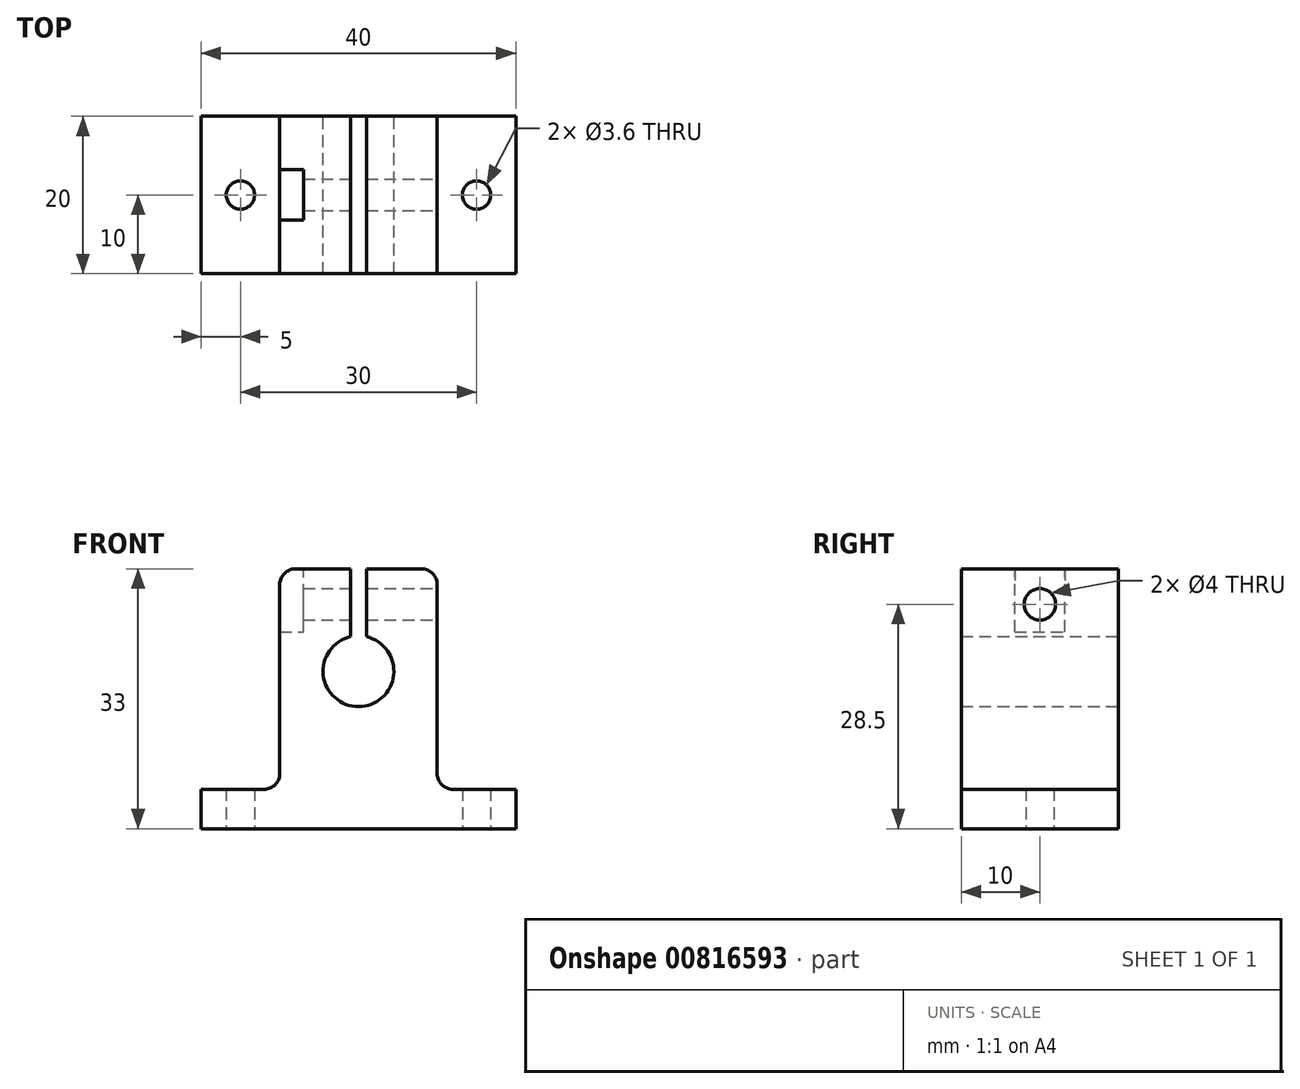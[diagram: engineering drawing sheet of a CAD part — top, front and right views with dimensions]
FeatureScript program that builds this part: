
annotation { "Feature Type Name" : "Feature", "Feature Type Description" : "" }
export const myFeature = defineFeature(function(context is Context, id is Id, definition is map)
    precondition{}
    {
        {
            var Q0;
            Q0=qCreatedBy(makeId("Front.planeOp"),FACE);
            var sketch = newSketch(context, id + "F0", { "sketchPlane" : qUnion([Q0])});
            skLineSegment(sketch, "E0", {"start": v(-10, 33) * mm, "end": v(10, 33) * mm});
            skLineSegment(sketch, "E1", {"start": v(10, 33) * mm, "end": v(10, 5) * mm});
            skLineSegment(sketch, "E2", {"start": v(10, 5) * mm, "end": v(20, 5) * mm});
            skLineSegment(sketch, "E3", {"start": v(20, 5) * mm, "end": v(20, 0) * mm});
            skLineSegment(sketch, "E4", {"start": v(20, 0) * mm, "end": v(-20, 0) * mm});
            skLineSegment(sketch, "E5", {"start": v(-20, 0) * mm, "end": v(-20, 5) * mm});
            skLineSegment(sketch, "E6", {"start": v(-20, 5) * mm, "end": v(-10, 5) * mm});
            skLineSegment(sketch, "E7", {"start": v(-10, 5) * mm, "end": v(-10, 33) * mm});
            skLineSegment(sketch, "E8", {"start": v(0, 33) * mm, "end": v(0, 0) * mm, "construction": true});
            skLineSegment(sketch, "E9", {"start": v(-1, 33) * mm, "end": v(-1, 20) * mm});
            skLineSegment(sketch, "E10", {"start": v(-1, 20) * mm, "end": v(0, 20) * mm});
            skCircle(sketch, "E11", {"center": v(0, 20) * mm, "radius": 4.5 * mm});
            skLineSegment(sketch, "E12.MirrorCS", {"start": v(1, 33) * mm, "end": v(1, 20) * mm});
            skLineSegment(sketch, "E13.MirrorCS", {"start": v(1, 20) * mm, "end": v(0, 20) * mm});
            skSolve(sketch);
        }
        {
            var Q0;
            {var subQ6=sQuery(id+"F0.wireOp",EDGE,"E1");Q0=makeQuery(id+"F0.imprint","IMPRINT",FACE,{"disambiguationData":[TD([[makeQuery(id+"F0.imprint","IMPRINT",EDGE,{"derivedFrom":subQ6}),-1.0]])]});}
            extrude(context, id + "F1", {"entities" : qUnion([Q0]), "depth" : 20 * mm, "offsetDistance" : 25 * mm});
        }
        {
            var Q0;
            Q0=makeQuery(id+"F1.opExtrude","SWEPT_FACE",FACE,{"disambiguationData":[OSD([sQuery(id+"F0.wireOp",EDGE,"E1")])]});
            var sketch = newSketch(context, id + "F2", { "sketchPlane" : qUnion([Q0])});
            skCircle(sketch, "E14", {"center": v(-10, 28.5) * mm, "radius": 2 * mm});
            skPoint(sketch, "E14.centerSnap0", {"position": v(-10, 33) * mm});
            skSolve(sketch);
        }
        {
            var Q0;
            Q0=makeQuery(id+"F2.imprint","IMPRINT",FACE,{"disambiguationData":[TD([[makeQuery(id+"F2.imprint","IMPRINT",EDGE,{"derivedFrom":sQuery(id+"F2.wireOp",EDGE,"E14")}),1.0]])]});
            extrude(context, id + "F3", {"entities" : qUnion([Q0]), "operationType" : NewBodyOperationType.REMOVE, "oppositeDirection" : true, "depth" : 25 * mm, "offsetDistance" : 25 * mm});
        }
        {
            var Q0;
            {var subQ0=sQuery(id+"F0.wireOp",EDGE,"E0");Q0=makeQuery(id+"F1.opExtrude","SWEPT_FACE",FACE,{"disambiguationData":[OSD([subQ0]),TDD([makeQuery(id+"F0.imprint","IMPRINT",EDGE,{"disambiguationData":[TD([[makeQuery(id+"F0.imprint","INTERSECT",VERTEX,{"derivedFrom":[subQ0,sQuery(id+"F0.wireOp",EDGE,"E7")]}),-1.0]])],"derivedFrom":subQ0})])]});}
            var sketch = newSketch(context, id + "F4", { "sketchPlane" : qUnion([Q0])});
            skLineSegment(sketch, "E15", {"start": v(-10, -10) * mm, "end": v(-1, -10) * mm, "construction": true});
            skLineSegment(sketch, "E16", {"start": v(-10, -6.8) * mm, "end": v(-7, -6.8) * mm});
            skLineSegment(sketch, "E17", {"start": v(-7, -6.8) * mm, "end": v(-7, -10) * mm});
            skLineSegment(sketch, "E18.MirrorCS", {"start": v(-7, -13.2) * mm, "end": v(-7, -10) * mm});
            skLineSegment(sketch, "E19.MirrorCS", {"start": v(-10, -13.2) * mm, "end": v(-7, -13.2) * mm});
            skSolve(sketch);
        }
        {
            var Q0;
            {var subQ1=sQuery(id+"F4.wireOp",EDGE,"E16");Q0=makeQuery(id+"F4.imprint","IMPRINT",FACE,{"disambiguationData":[TD([[makeQuery(id+"F4.imprint","IMPRINT",EDGE,{"derivedFrom":subQ1}),-1.0]])]});}
            extrude(context, id + "F5", {"entities" : qUnion([Q0]), "operationType" : NewBodyOperationType.REMOVE, "oppositeDirection" : true, "depth" : 8 * mm, "offsetDistance" : 25 * mm});
        }
        {
            var Q0;
            Q0=makeQuery(id+"F1.opExtrude","SWEPT_FACE",FACE,{"disambiguationData":[OSD([sQuery(id+"F0.wireOp",EDGE,"E4")])]});
            var sketch = newSketch(context, id + "F6", { "sketchPlane" : qUnion([Q0])});
            skLineSegment(sketch, "E20", {"start": v(-20, 10) * mm, "end": v(20, 10) * mm, "construction": true});
            skCircle(sketch, "E21", {"center": v(-15, 10) * mm, "radius": 1.8 * mm});
            skCircle(sketch, "E22", {"center": v(15, 10) * mm, "radius": 1.8 * mm});
            skSolve(sketch);
        }
        {
            var Q0;
            Q0=makeQuery(id+"F6.imprint","IMPRINT",FACE,{"disambiguationData":[TD([[makeQuery(id+"F6.imprint","IMPRINT",EDGE,{"derivedFrom":sQuery(id+"F6.wireOp",EDGE,"E21")}),1.0]])]});
            var Q1;
            Q1=makeQuery(id+"F6.imprint","IMPRINT",FACE,{"disambiguationData":[TD([[makeQuery(id+"F6.imprint","IMPRINT",EDGE,{"derivedFrom":sQuery(id+"F6.wireOp",EDGE,"E22")}),1.0]])]});
            extrude(context, id + "F7", {"entities" : qUnion([Q0, Q1]), "operationType" : NewBodyOperationType.REMOVE, "oppositeDirection" : true, "depth" : 25 * mm, "offsetDistance" : 25 * mm});
        }
        {
            var Q0;
            Q0=makeQuery(id+"F1.opExtrude","SWEPT_EDGE",EDGE,{"disambiguationData":[OSD([sQuery(id+"F0.wireOp",EDGE,"E6"),sQuery(id+"F0.wireOp",EDGE,"E7")])]});
            var Q1;
            Q1=makeQuery(id+"F1.opExtrude","SWEPT_EDGE",EDGE,{"disambiguationData":[OSD([sQuery(id+"F0.wireOp",EDGE,"E1"),sQuery(id+"F0.wireOp",EDGE,"E2")])]});
            var Q2;
            {var subQ0=sQuery(id+"F0.wireOp",EDGE,"E7");var subQ1=sQuery(id+"F0.wireOp",EDGE,"E0");Q2=makeQuery(id+"F5.boolean.opBoolean","SPLIT",EDGE,{"disambiguationData":[TD([makeQuery(id+"F5.opExtrude","SWEPT_FACE",FACE,{"disambiguationData":[OSD([sQuery(id+"F4.wireOp",EDGE,"E19.MirrorCS")])]})])],"derivedFrom":makeQuery(id+"F1.opExtrude","SWEPT_EDGE",EDGE,{"disambiguationData":[OSD([subQ1,subQ0])]})});}
            var Q3;
            Q3=makeQuery(id+"F1.opExtrude","SWEPT_EDGE",EDGE,{"disambiguationData":[OSD([sQuery(id+"F0.wireOp",EDGE,"E0"),sQuery(id+"F0.wireOp",EDGE,"E1")])]});
            var Q4;
            {var subQ0=sQuery(id+"F0.wireOp",EDGE,"E7");var subQ1=sQuery(id+"F0.wireOp",EDGE,"E0");Q4=makeQuery(id+"F5.boolean.opBoolean","SPLIT",EDGE,{"disambiguationData":[TD([makeQuery(id+"F5.opExtrude","SWEPT_FACE",FACE,{"disambiguationData":[OSD([sQuery(id+"F4.wireOp",EDGE,"E16")])]})])],"derivedFrom":makeQuery(id+"F1.opExtrude","SWEPT_EDGE",EDGE,{"disambiguationData":[OSD([subQ1,subQ0])]})});}
            fillet(context, id + "F8", {"entities" : qUnion([Q0, Q1, Q2, Q3, Q4]), "radius" : 2 * mm, "tangentPropagation" : true, "allowEdgeOverflow" : false});
        }
    });
